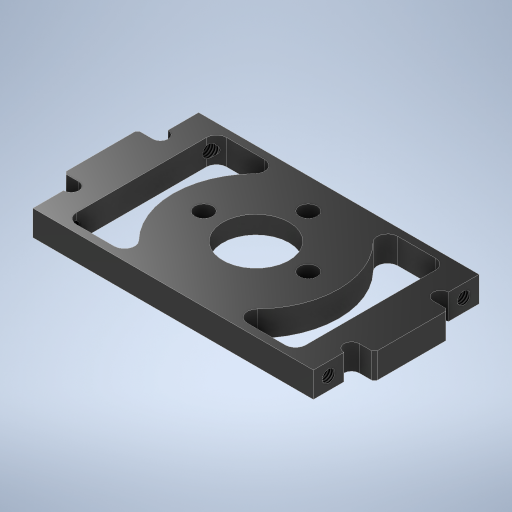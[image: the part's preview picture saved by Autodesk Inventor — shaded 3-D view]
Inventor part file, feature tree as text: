
AUTODESK INVENTOR PART (.ipt)
format: ipt  version: 2024.2 (Build 282272000, 272)  size: 413,184 bytes
history: native  units: mm
features: hole x3, sketch x2, extrude x2, fillet x1, chamfer x1, mirror x1
ambient origin geometry x8: Origin, YZ Plane, XZ Plane, XY Plane, X Axis, Y Axis, Z Axis, Center Point
bodies: Solid1 (feature_tree)
feature tree (10):
  sketch  "Sketch1"  dims[d1=40.0mm d3=40.0mm d9=360.0deg d10=20.5mm d11=29.5mm d12=25.0mm d13=0.05mm d14=360.0deg d19=32.5mm]
  extrude  "Extrusion1"  Depth=32.5mm
  extrude  "Extrusion2"  Depth=5.0mm
  fillet  "Fillet1"  Radius=3.0mm
  hole  "Hole1"  [1 undecoded]
  hole  "Hole2"  [1 undecoded]
  hole  "Hole3"  [1 undecoded]
  chamfer  "Chamfer1"  Distance=1.5mm
  mirror  "Mirror1"
  sketch  "Sketch2"  dims[d20=55.0mm d21=1.5mm d23=3.0mm d24=6.0mm d25=6.0mm d27=5.0mm d28=0.0mm d29=1.5mm d30=0.0mm d31=2.0mm d32=2.459mm d33=6.0mm d34=4.0mm d35=2.0mm d36=90.0deg d37=6.0mm d38=0.0mm d39=3.5mm d40=6.0mm d41=4.0mm d42=2.0mm d43=90.0deg d44=6.0mm d45=0.0mm d46=13.0mm d47=6.0mm d48=4.0mm d49=2.0mm d50=90.0deg d51=8.0mm d52=0.0mm d53=0.5mm d54=2.0mm d55=45.0deg d56=3.0mm d57=5.0mm]
note: 3 required parameter values undecoded (feature->parameter linkage not recoverable at this tier; creation-order binding heuristic only, values carry confidence <= 0.55)
